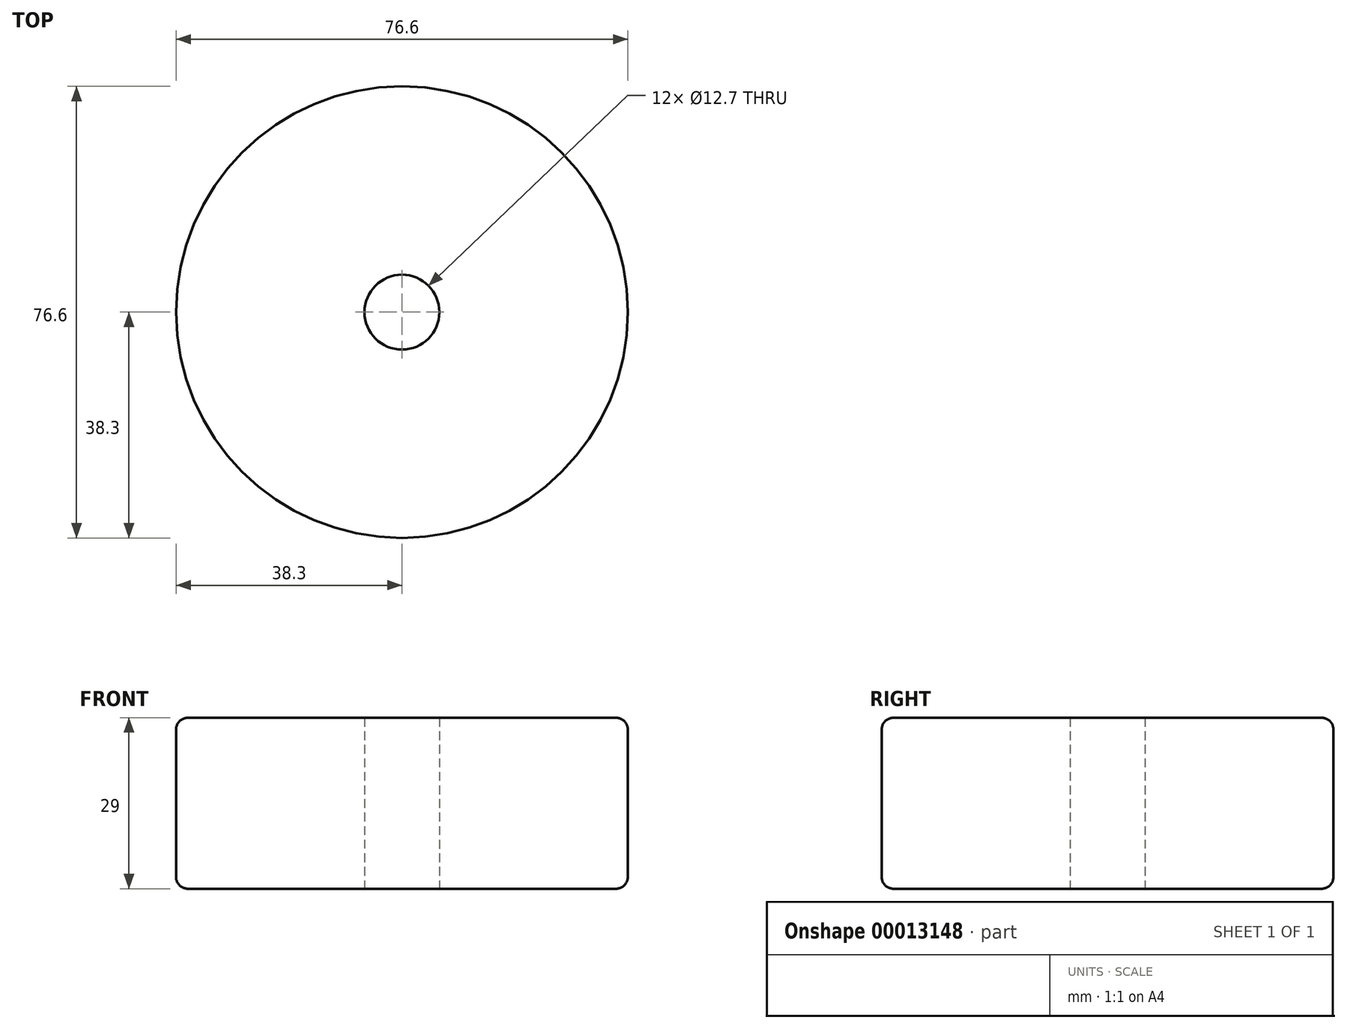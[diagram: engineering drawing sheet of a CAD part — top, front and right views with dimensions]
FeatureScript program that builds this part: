
annotation { "Feature Type Name" : "Feature", "Feature Type Description" : "" }
export const myFeature = defineFeature(function(context is Context, id is Id, definition is map)
    precondition{}
    {
        {
            var Q0;
            Q0=qCreatedBy(makeId("Top.planeOp"),FACE);
            var sketch = newSketch(context, id + "F0", { "sketchPlane" : qUnion([Q0])});
            skCircle(sketch, "E0", {"center": v(0, 0) * mm, "radius": 38.3 * mm});
            skCircle(sketch, "E1", {"center": v(0, 0) * mm, "radius": 6.35 * mm});
            skSolve(sketch);
        }
        {
            var Q0;
            Q0=makeQuery(id+"F0.imprint","IMPRINT",FACE,{"disambiguationData":[TD([[makeQuery(id+"F0.imprint","IMPRINT",EDGE,{"derivedFrom":sQuery(id+"F0.wireOp",EDGE,"E0")}),1.0]])]});
            extrude(context, id + "F1", {"entities" : qUnion([Q0]), "depth" : 29 * mm});
        }
        {
            var Q0;
            Q0=makeQuery(id+"F1.opExtrude","SWEPT_FACE",FACE,{"disambiguationData":[OSD([sQuery(id+"F0.wireOp",EDGE,"E0")])]});
            fillet(context, id + "F2", {"entities" : qUnion([Q0]), "radius" : 2 * mm, "tangentPropagation" : true, "allowEdgeOverflow" : false});
        }
    });
